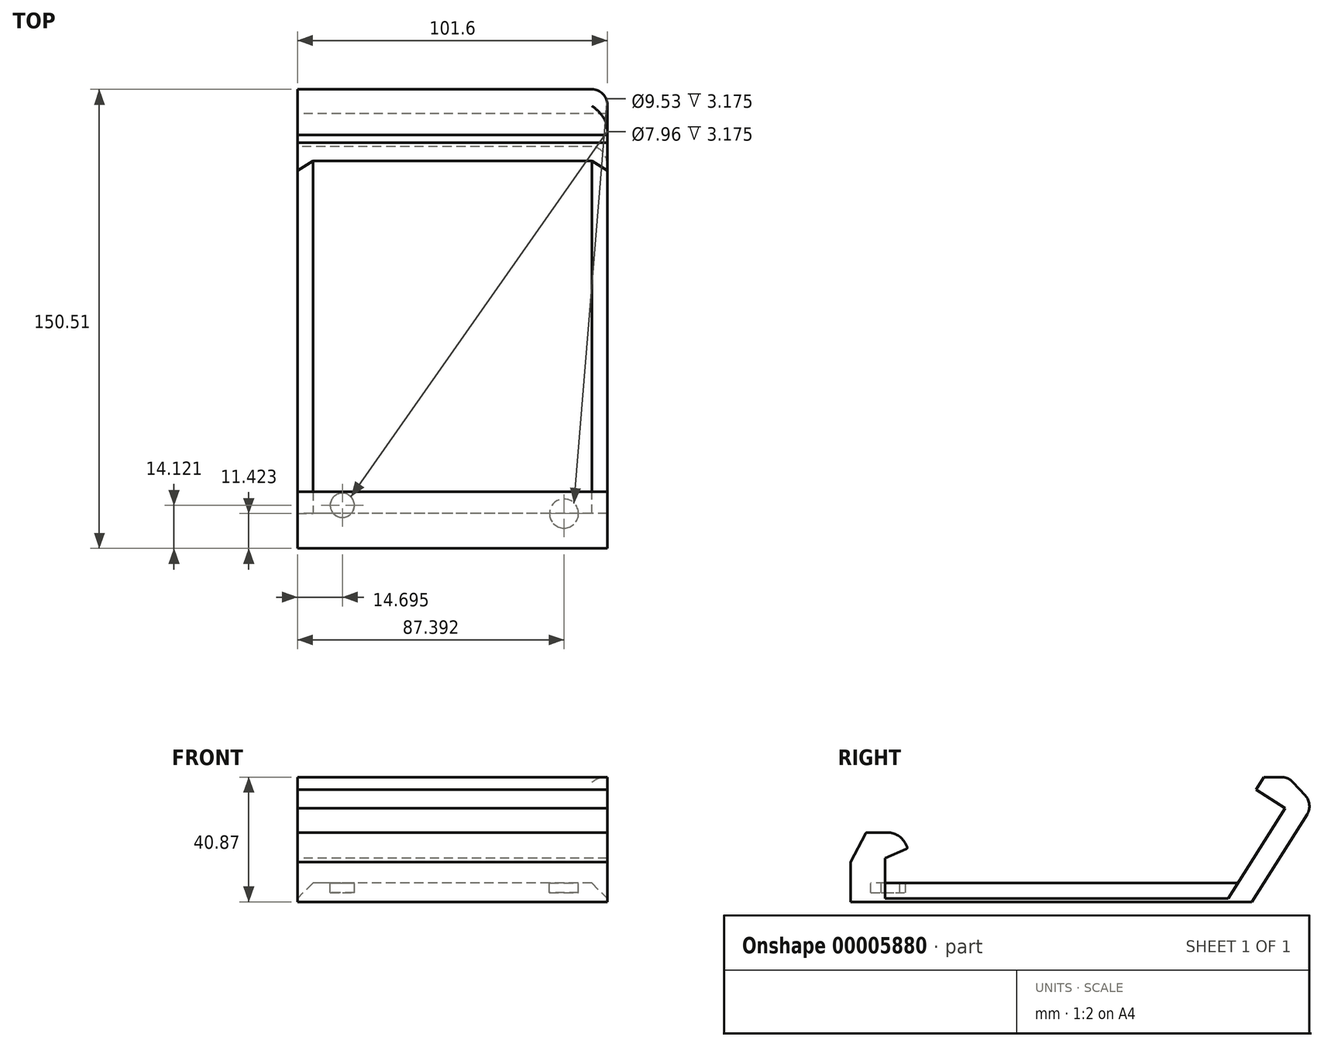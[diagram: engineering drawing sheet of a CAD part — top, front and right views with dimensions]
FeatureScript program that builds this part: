
annotation { "Feature Type Name" : "Feature", "Feature Type Description" : "" }
export const myFeature = defineFeature(function(context is Context, id is Id, definition is map)
    precondition{}
    {
        {
            var Q0;
            Q0=qCreatedBy(makeId("Right.planeOp"),FACE);
            var sketch = newSketch(context, id + "F0", { "sketchPlane" : qUnion([Q0])});
            skLineSegment(sketch, "E0", {"start": v(-52.7, 0.43) * mm, "end": v(-53.31, 1.68) * mm});
            skLineSegment(sketch, "E1", {"start": v(-59, 5.19) * mm, "end": v(-65.79, 5.19) * mm});
            skLineSegment(sketch, "E2", {"start": v(-66.2, 4.95) * mm, "end": v(-71.25, -4.54) * mm});
            skLineSegment(sketch, "E3", {"start": v(-71.25, -4.54) * mm, "end": v(-71.25, -17.52) * mm});
            skLineSegment(sketch, "E4", {"start": v(-71.25, -17.52) * mm, "end": v(60.44, -17.52) * mm});
            skLineSegment(sketch, "E5", {"start": v(60.44, -17.52) * mm, "end": v(80.55, 14.49) * mm});
            skLineSegment(sketch, "E6", {"start": v(80.55, 14.49) * mm, "end": v(72.33, 23.35) * mm});
            skLineSegment(sketch, "E7", {"start": v(72.33, 23.35) * mm, "end": v(64.33, 23.35) * mm});
            skLineSegment(sketch, "E8", {"start": v(64.33, 23.35) * mm, "end": v(61.74, 19.25) * mm});
            skLineSegment(sketch, "E9", {"start": v(61.74, 19.25) * mm, "end": v(71.32, 13.2) * mm});
            skLineSegment(sketch, "E10", {"start": v(71.32, 13.2) * mm, "end": v(55.83, -11.33) * mm});
            skLineSegment(sketch, "E11", {"start": v(55.83, -11.33) * mm, "end": v(-59.83, -11.33) * mm});
            skLineSegment(sketch, "E12", {"start": v(-59.83, -11.33) * mm, "end": v(-59.83, -3.24) * mm});
            skLineSegment(sketch, "E13", {"start": v(-59.83, -3.24) * mm, "end": v(-52.92, -0.2) * mm});
            skPoint(sketch, "E14.visualSharp", {"position": v(-52.47, 0) * mm});
            skArc(sketch, "E14.filletArc", {"start": v(-52.92, -0.2) * mm, "mid": v(-52.67, 0.07) * mm, "end": v(-52.7, 0.43) * mm});
            skPoint(sketch, "E15.visualSharp", {"position": v(-66.06, 5.19) * mm});
            skArc(sketch, "E15.filletArc", {"start": v(-65.79, 5.19) * mm, "mid": v(-66.02, 5.12) * mm, "end": v(-66.2, 4.95) * mm});
            skPoint(sketch, "E16.visualSharp", {"position": v(-55.07, 5.19) * mm});
            skArc(sketch, "E16.filletArc", {"start": v(-53.31, 1.68) * mm, "mid": v(-55.66, 4.24) * mm, "end": v(-59, 5.19) * mm});
            skSolve(sketch);
        }
        {
            var Q0;
            Q0 = qSketchRegion(id + "F0", true);
            extrude(context, id + "F1", {"entities" : qUnion([Q0]), "depth" : 101.6 * mm});
        }
        {
            var Q0;
            Q0=makeQuery(id+"F1.opExtrude","SWEPT_FACE",FACE,{"disambiguationData":[OSD([sQuery(id+"F0.wireOp",EDGE,"E11")])]});
            var sketch = newSketch(context, id + "F2", { "sketchPlane" : qUnion([Q0])});
            skCircle(sketch, "E17", {"center": v(14.7, -57.13) * mm, "radius": 3.98 * mm});
            skCircle(sketch, "E18", {"center": v(87.4, -59.83) * mm, "radius": 4.77 * mm});
            skSolve(sketch);
        }
        {
            var Q0;
            Q0 = qSketchRegion(id + "F2", true);
            extrude(context, id + "F3", {"entities" : qUnion([Q0]), "operationType" : NewBodyOperationType.REMOVE, "oppositeDirection" : true, "depth" : 3.17 * mm});
        }
        {
            var Q0;
            Q0=makeQuery(id+"F1.opExtrude","CAP_EDGE",EDGE,{"disambiguationData":[OSD([sQuery(id+"F0.wireOp",EDGE,"E11")])],"isStart":true});
            chamfer(context, id + "F4", {"entities" : qUnion([Q0]), "width" : 5.08 * mm, "tangentPropagation" : true});
        }
        {
            var Q0;
            Q0=makeQuery(id+"F1.opExtrude","CAP_EDGE",EDGE,{"disambiguationData":[OSD([sQuery(id+"F0.wireOp",EDGE,"E11")])],"isStart":false});
            chamfer(context, id + "F5", {"entities" : qUnion([Q0]), "width" : 5.08 * mm, "tangentPropagation" : true});
        }
        {
            var Q0;
            Q0=makeQuery(id+"F1.opExtrude","CAP_EDGE",EDGE,{"disambiguationData":[OSD([sQuery(id+"F0.wireOp",EDGE,"E5")])],"isStart":false});
            var Q1;
            Q1=makeQuery(id+"F1.opExtrude","CAP_EDGE",EDGE,{"disambiguationData":[OSD([sQuery(id+"F0.wireOp",EDGE,"E6")])],"isStart":false});
            var Q2;
            Q2=makeQuery(id+"F1.opExtrude","SWEPT_EDGE",EDGE,{"disambiguationData":[OSD([sQuery(id+"F0.wireOp",EDGE,"E6"),sQuery(id+"F0.wireOp",EDGE,"E7")])]});
            var Q3;
            Q3=makeQuery(id+"F1.opExtrude","SWEPT_EDGE",EDGE,{"disambiguationData":[OSD([sQuery(id+"F0.wireOp",EDGE,"E5"),sQuery(id+"F0.wireOp",EDGE,"E6")])]});
            fillet(context, id + "F6", {"entities" : qUnion([Q0, Q1, Q2, Q3]), "radius" : 5.08 * mm, "tangentPropagation" : true, "allowEdgeOverflow" : false});
        }
    });
